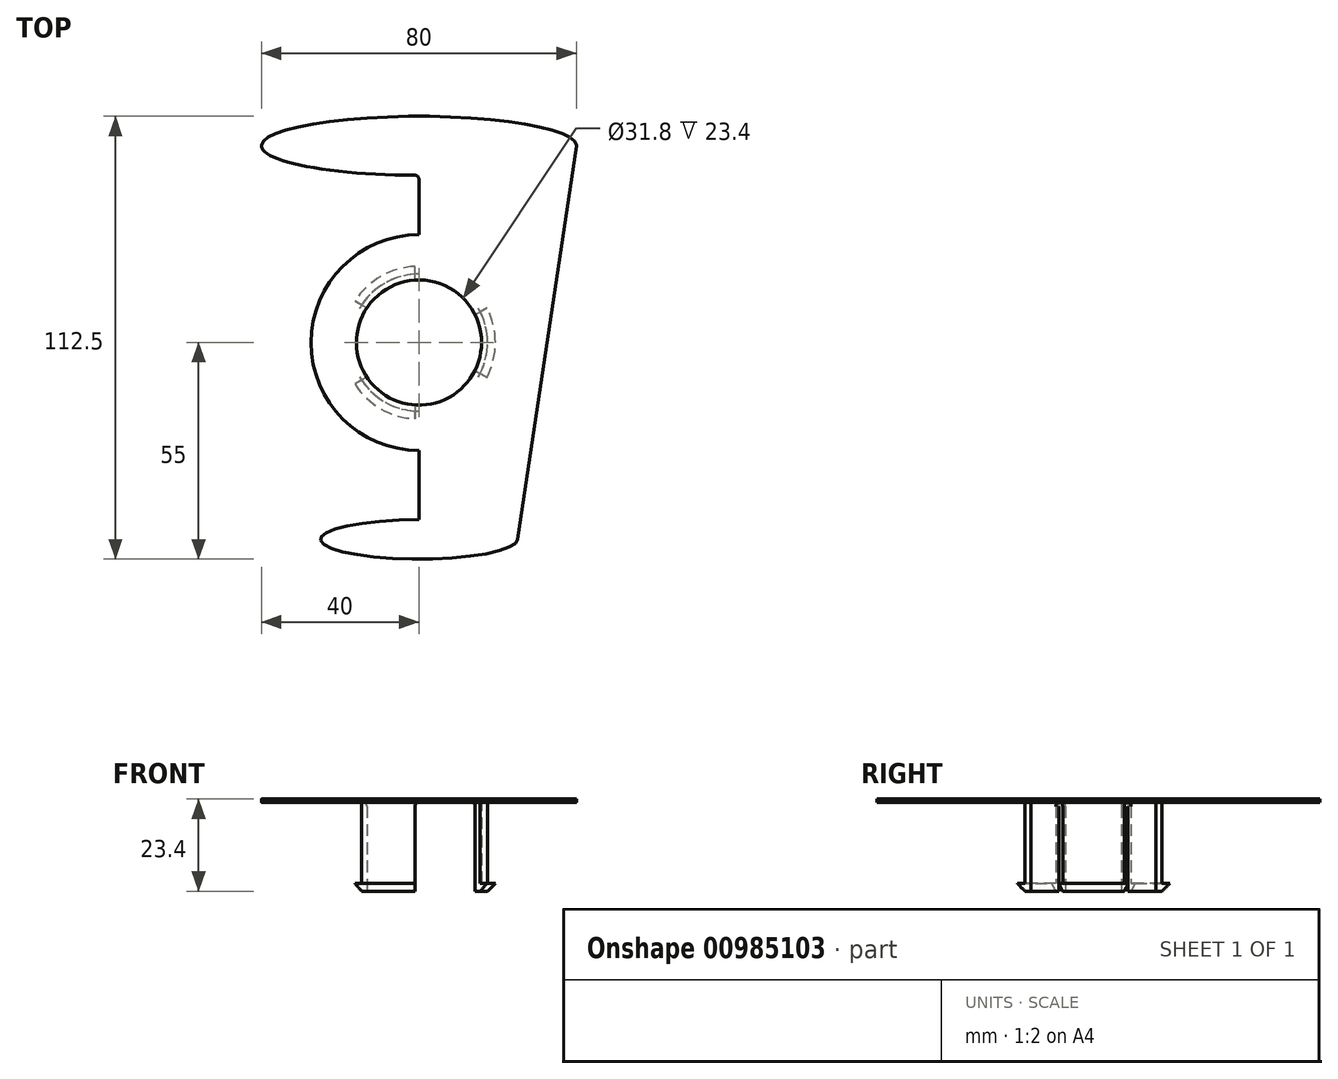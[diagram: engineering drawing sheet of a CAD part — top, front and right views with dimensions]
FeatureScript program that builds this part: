
annotation { "Feature Type Name" : "Feature", "Feature Type Description" : "" }
export const myFeature = defineFeature(function(context is Context, id is Id, definition is map)
    precondition{}
    {
        {
            var Q0;
            Q0=qCreatedBy(makeId("Top.planeOp"),FACE);
            var sketch = newSketch(context, id + "F0", { "sketchPlane" : qUnion([Q0])});
            skCircle(sketch, "E0", {"center": v(0, 0) * mm, "radius": 17.4 * mm});
            skCircle(sketch, "E1", {"center": v(0, 0) * mm, "radius": 15.9 * mm});
            skCircle(sketch, "E2", {"center": v(0, 0) * mm, "radius": 27.4 * mm});
            skLineSegment(sketch, "E3", {"start": v(0, 0) * mm, "end": v(0, 17.75) * mm, "construction": true});
            skText(sketch, "E4", { "text": "o", "fontName": "RobotoSlab-Bold.ttf"});
            skText(sketch, "E5", { "text": "u", "fontName": "RobotoSlab-Bold.ttf"});
            skText(sketch, "E6", { "text": "e", "fontName": "RobotoSlab-Bold.ttf"});
            skText(sketch, "E7", { "text": "i", "fontName": "RobotoSlab-Bold.ttf"});
            skText(sketch, "E8", { "text": "r", "fontName": "RobotoSlab-Bold.ttf"});
            skText(sketch, "E9", { "text": "c", "fontName": "RobotoSlab-Bold.ttf"});
            skText(sketch, "E10", { "text": "e", "fontName": "RobotoSlab-Bold.ttf"});
            skText(sketch, "E11", { "text": "o", "fontName": "RobotoSlab-Bold.ttf"});
            skText(sketch, "E12", { "text": "r", "fontName": "RobotoSlab-Bold.ttf"});
            skText(sketch, "E13", { "text": "n", "fontName": "RobotoSlab-Bold.ttf"});
            skLineSegment(sketch, "E14.2.0", {"start": v(0, 0) * mm, "end": v(-15.37, 8.88) * mm, "construction": true});
            skLineSegment(sketch, "E14.3.0", {"start": v(0, 0) * mm, "end": v(-17.75, 0) * mm, "construction": true});
            skLineSegment(sketch, "E14.4.0", {"start": v(0, 0) * mm, "end": v(-15.37, -8.88) * mm, "construction": true});
            skLineSegment(sketch, "E14.5.0", {"start": v(0, 0) * mm, "end": v(-8.88, -15.37) * mm, "construction": true});
            skLineSegment(sketch, "E14.6.0", {"start": v(0, 0) * mm, "end": v(0, -17.75) * mm, "construction": true});
            skLineSegment(sketch, "E14.7.0", {"start": v(0, 0) * mm, "end": v(8.87, -15.37) * mm, "construction": true});
            skLineSegment(sketch, "E14.8.0", {"start": v(0, 0) * mm, "end": v(15.37, -8.88) * mm, "construction": true});
            skLineSegment(sketch, "E14.9.0", {"start": v(0, 0) * mm, "end": v(17.75, 0) * mm, "construction": true});
            skLineSegment(sketch, "E14.10.0", {"start": v(0, 0) * mm, "end": v(15.37, 8.87) * mm, "construction": true});
            skLineSegment(sketch, "E14.11.0", {"start": v(0, 0) * mm, "end": v(8.88, 15.37) * mm, "construction": true});
            skText(sketch, "E15", { "text": "S", "fontName": "RobotoSlab-Bold.ttf"});
            skLineSegment(sketch, "E16", {"start": v(0, 0) * mm, "end": v(-8.88, 15.37) * mm, "construction": true});
            const initialGuessF0  = {"E4": [-0.00328, 0.01775, 1, 0, 0.008], "E5": [0.0057, 0.0172, 0.86603, -0.5, 0.008], "E6": [0.01692, -0.0062, -0.5, -0.86603, 0.008], "E7": [-0.0071, -0.0164, -0.86603, 0.5, 0.008], "E8": [-0.01407, -0.01114, -0.5, 0.86603, 0.008], "E9": [0.01775, 0.0031, 0, -1, 0.008], "E10": [0.01156, -0.01382, -0.86603, -0.5, 0.008], "E11": [-0.01775, -0.00328, 0, 1, 0.008], "E12": [0.01407, 0.01114, 0.5, -0.86603, 0.008], "E13": [-0.01726, 0.0056, 0.5, 0.86603, 0.008], "E15": [-0.01195, 0.0136, 0.86603, 0.5, 0.008]};
            skSetInitialGuess(sketch, initialGuessF0);
            skSolve(sketch);
        }
        {
            var Q0;
            Q0=makeQuery(id+"F0.imprint","IMPRINT",FACE,{"disambiguationData":[TD([[makeQuery(id+"F0.imprint","IMPRINT",EDGE,{"derivedFrom":sQuery(id+"F0.wireOp",EDGE,"E0")}),1.0]])]});
            var Q1;
            Q1=makeQuery(id+"F0.imprint","IMPRINT",FACE,{"disambiguationData":[TD([[makeQuery(id+"F0.imprint","IMPRINT",EDGE,{"derivedFrom":sQuery(id+"F0.wireOp",EDGE,"E4.sketch_text.stroke-0")}),-1.0]])]});
            var Q2;
            Q2=makeQuery(id+"F0.imprint","IMPRINT",FACE,{"disambiguationData":[TD([[makeQuery(id+"F0.imprint","IMPRINT",EDGE,{"derivedFrom":sQuery(id+"F0.wireOp",EDGE,"E7.sketch_text.stroke-0")}),-1.0]])]});
            var Q3;
            Q3=makeQuery(id+"F0.imprint","IMPRINT",FACE,{"disambiguationData":[TD([[makeQuery(id+"F0.imprint","IMPRINT",EDGE,{"derivedFrom":sQuery(id+"F0.wireOp",EDGE,"E11.sketch_text.stroke-10")}),1.0]])]});
            var Q4;
            Q4=makeQuery(id+"F0.imprint","IMPRINT",FACE,{"disambiguationData":[TD([[makeQuery(id+"F0.imprint","IMPRINT",EDGE,{"derivedFrom":sQuery(id+"F0.wireOp",EDGE,"E9.sketch_text.stroke-0")}),-1.0]])]});
            var Q5;
            Q5=makeQuery(id+"F0.imprint","IMPRINT",FACE,{"disambiguationData":[TD([[makeQuery(id+"F0.imprint","IMPRINT",EDGE,{"derivedFrom":sQuery(id+"F0.wireOp",EDGE,"E10.sketch_text.stroke-0")}),-1.0]])]});
            var Q6;
            Q6=makeQuery(id+"F0.imprint","IMPRINT",FACE,{"disambiguationData":[TD([[makeQuery(id+"F0.imprint","IMPRINT",EDGE,{"derivedFrom":sQuery(id+"F0.wireOp",EDGE,"E6.sketch_text.stroke-0")}),-1.0]])]});
            var Q7;
            Q7=makeQuery(id+"F0.imprint","IMPRINT",FACE,{"disambiguationData":[TD([[makeQuery(id+"F0.imprint","IMPRINT",EDGE,{"derivedFrom":sQuery(id+"F0.wireOp",EDGE,"E12.sketch_text.stroke-0")}),-1.0]])]});
            var Q8;
            Q8=makeQuery(id+"F0.imprint","IMPRINT",FACE,{"disambiguationData":[TD([[makeQuery(id+"F0.imprint","IMPRINT",EDGE,{"derivedFrom":sQuery(id+"F0.wireOp",EDGE,"E5.sketch_text.stroke-0")}),-1.0]])]});
            var Q9;
            Q9=makeQuery(id+"F0.imprint","IMPRINT",FACE,{"disambiguationData":[TD([[makeQuery(id+"F0.imprint","IMPRINT",EDGE,{"derivedFrom":sQuery(id+"F0.wireOp",EDGE,"E0")}),-1.0]])]});
            var Q10;
            Q10=makeQuery(id+"F0.imprint","IMPRINT",FACE,{"disambiguationData":[TD([[makeQuery(id+"F0.imprint","IMPRINT",EDGE,{"derivedFrom":sQuery(id+"F0.wireOp",EDGE,"E5.sketch_text.stroke-10")}),1.0]])]});
            var Q11;
            Q11=makeQuery(id+"F0.imprint","IMPRINT",FACE,{"disambiguationData":[TD([[makeQuery(id+"F0.imprint","IMPRINT",EDGE,{"derivedFrom":sQuery(id+"F0.wireOp",EDGE,"E13.sketch_text.stroke-0")}),-1.0]])]});
            var Q12;
            Q12=makeQuery(id+"F0.imprint","IMPRINT",FACE,{"disambiguationData":[TD([[makeQuery(id+"F0.imprint","IMPRINT",EDGE,{"derivedFrom":sQuery(id+"F0.wireOp",EDGE,"E8.sketch_text.stroke-0")}),-1.0]])]});
            var Q13;
            Q13=makeQuery(id+"F0.imprint","IMPRINT",FACE,{"disambiguationData":[TD([[makeQuery(id+"F0.imprint","IMPRINT",EDGE,{"derivedFrom":sQuery(id+"F0.wireOp",EDGE,"E11.sketch_text.stroke-0")}),-1.0]])]});
            var Q14;
            Q14=makeQuery(id+"F0.imprint","IMPRINT",FACE,{"disambiguationData":[TD([[makeQuery(id+"F0.imprint","IMPRINT",EDGE,{"derivedFrom":sQuery(id+"F0.wireOp",EDGE,"E7.sketch_text.stroke-10")}),-1.0]])]});
            var Q15;
            Q15=makeQuery(id+"F0.imprint","IMPRINT",FACE,{"disambiguationData":[TD([[makeQuery(id+"F0.imprint","IMPRINT",EDGE,{"derivedFrom":sQuery(id+"F0.wireOp",EDGE,"E10.sketch_text.stroke-17")}),1.0]])]});
            var Q16;
            Q16=makeQuery(id+"F0.imprint","IMPRINT",FACE,{"disambiguationData":[TD([[makeQuery(id+"F0.imprint","IMPRINT",EDGE,{"derivedFrom":sQuery(id+"F0.wireOp",EDGE,"E15.sketch_text.stroke-0")}),-1.0]])]});
            var Q17;
            Q17=makeQuery(id+"F0.imprint","IMPRINT",FACE,{"disambiguationData":[TD([[makeQuery(id+"F0.imprint","IMPRINT",EDGE,{"derivedFrom":sQuery(id+"F0.wireOp",EDGE,"E4.sketch_text.stroke-10")}),1.0]])]});
            var Q18;
            Q18=makeQuery(id+"F0.imprint","IMPRINT",FACE,{"disambiguationData":[TD([[makeQuery(id+"F0.imprint","IMPRINT",EDGE,{"derivedFrom":sQuery(id+"F0.wireOp",EDGE,"E6.sketch_text.stroke-17")}),1.0]])]});
            extrude(context, id + "F1", {"entities" : qUnion([Q0, Q1, Q2, Q3, Q4, Q5, Q6, Q7, Q8, Q9, Q10, Q11, Q12, Q13, Q14, Q15, Q16, Q17, Q18]), "depth" : 0.8 * mm, "offsetDistance" : 25 * mm});
        }
        {
            var Q0;
            Q0=makeQuery(id+"F0.imprint","IMPRINT",FACE,{"disambiguationData":[TD([[makeQuery(id+"F0.imprint","IMPRINT",EDGE,{"derivedFrom":sQuery(id+"F0.wireOp",EDGE,"E0")}),1.0]])]});
            extrude(context, id + "F2", {"entities" : qUnion([Q0]), "operationType" : NewBodyOperationType.ADD, "oppositeDirection" : true, "depth" : 22.6 * mm, "offsetDistance" : 25 * mm});
        }
        {
            var Q0;
            Q0=makeQuery(id+"F2.opExtrude","CAP_FACE",FACE,{"disambiguationData":[OSD([sQuery(id+"F0.wireOp",EDGE,"E0"),sQuery(id+"F0.wireOp",EDGE,"E1")])],"isStart":false});
            var sketch = newSketch(context, id + "F3", { "sketchPlane" : qUnion([Q0])});
            skLineSegment(sketch, "E17.bottom", {"start": v(1, 0) * mm, "end": v(-1, 0) * mm});
            skLineSegment(sketch, "E17.top", {"start": v(1, -20) * mm, "end": v(-1, -20) * mm});
            skLineSegment(sketch, "E17.left", {"start": v(1, 0) * mm, "end": v(1, -20) * mm});
            skLineSegment(sketch, "E17.right", {"start": v(-1, 0) * mm, "end": v(-1, -20) * mm});
            skLineSegment(sketch, "E18.1.0", {"start": v(0.5, 0.87) * mm, "end": v(-0.5, -0.87) * mm});
            skLineSegment(sketch, "E18.1.1", {"start": v(17.82, -9.13) * mm, "end": v(16.82, -10.87) * mm});
            skLineSegment(sketch, "E18.1.2", {"start": v(-0.5, -0.87) * mm, "end": v(16.82, -10.87) * mm});
            skLineSegment(sketch, "E18.1.3", {"start": v(0.5, 0.87) * mm, "end": v(17.82, -9.13) * mm});
            skLineSegment(sketch, "E18.2.0", {"start": v(-0.5, 0.87) * mm, "end": v(0.5, -0.87) * mm});
            skLineSegment(sketch, "E18.2.1", {"start": v(16.82, 10.87) * mm, "end": v(17.82, 9.13) * mm});
            skLineSegment(sketch, "E18.2.2", {"start": v(0.5, -0.87) * mm, "end": v(17.82, 9.13) * mm});
            skLineSegment(sketch, "E18.2.3", {"start": v(-0.5, 0.87) * mm, "end": v(16.82, 10.87) * mm});
            skLineSegment(sketch, "E18.3.0", {"start": v(-1, 0) * mm, "end": v(1, 0) * mm});
            skLineSegment(sketch, "E18.3.1", {"start": v(-1, 20) * mm, "end": v(1, 20) * mm});
            skLineSegment(sketch, "E18.3.2", {"start": v(1, 0) * mm, "end": v(1, 20) * mm});
            skLineSegment(sketch, "E18.3.3", {"start": v(-1, 0) * mm, "end": v(-1, 20) * mm});
            skLineSegment(sketch, "E18.4.0", {"start": v(-0.5, -0.87) * mm, "end": v(0.5, 0.87) * mm});
            skLineSegment(sketch, "E18.4.1", {"start": v(-17.82, 9.13) * mm, "end": v(-16.82, 10.87) * mm});
            skLineSegment(sketch, "E18.4.2", {"start": v(0.5, 0.87) * mm, "end": v(-16.82, 10.87) * mm});
            skLineSegment(sketch, "E18.4.3", {"start": v(-0.5, -0.87) * mm, "end": v(-17.82, 9.13) * mm});
            skLineSegment(sketch, "E18.5.0", {"start": v(0.5, -0.87) * mm, "end": v(-0.5, 0.87) * mm});
            skLineSegment(sketch, "E18.5.1", {"start": v(-16.82, -10.87) * mm, "end": v(-17.82, -9.13) * mm});
            skLineSegment(sketch, "E18.5.2", {"start": v(-0.5, 0.87) * mm, "end": v(-17.82, -9.13) * mm});
            skLineSegment(sketch, "E18.5.3", {"start": v(0.5, -0.87) * mm, "end": v(-16.82, -10.87) * mm});
            skPoint(sketch, "E18.center", {"position": v(0, 0) * mm});
            skCircle(sketch, "E19", {"center": v(0, 0) * mm, "radius": 19.4 * mm});
            skSolve(sketch);
        }
        {
            var Q0;
            {var subQ0=sQuery(id+"F3.wireOp",EDGE,"E18.1.2");var subQ1=makeQuery(id+"F2.opExtrude","CAP_EDGE",EDGE,{"disambiguationData":[OSD([sQuery(id+"F0.wireOp",EDGE,"E1")])],"isStart":false});var subQ2=makeQuery(id+"F3.imprint","INTERSECT",VERTEX,{"derivedFrom":[subQ1,subQ0]});Q0=makeQuery(id+"F3.imprint","IMPRINT",FACE,{"disambiguationData":[TD([[makeQuery(id+"F3.imprint","IMPRINT",EDGE,{"disambiguationData":[TD([[subQ2,-1.0]])],"derivedFrom":subQ0}),1.0]])]});}
            var Q1;
            {var subQ0=sQuery(id+"F3.wireOp",EDGE,"E17.left");var subQ1=makeQuery(id+"F2.opExtrude","CAP_EDGE",EDGE,{"disambiguationData":[OSD([sQuery(id+"F0.wireOp",EDGE,"E1")])],"isStart":false});var subQ2=makeQuery(id+"F3.imprint","INTERSECT",VERTEX,{"derivedFrom":[subQ1,subQ0]});Q1=makeQuery(id+"F3.imprint","IMPRINT",FACE,{"disambiguationData":[TD([[makeQuery(id+"F3.imprint","IMPRINT",EDGE,{"disambiguationData":[TD([[subQ2,-1.0]])],"derivedFrom":subQ0}),-1.0]])]});}
            var Q2;
            {var subQ0=sQuery(id+"F3.wireOp",EDGE,"E18.5.2");var subQ1=makeQuery(id+"F2.opExtrude","CAP_EDGE",EDGE,{"disambiguationData":[OSD([sQuery(id+"F0.wireOp",EDGE,"E1")])],"isStart":false});var subQ2=makeQuery(id+"F3.imprint","INTERSECT",VERTEX,{"derivedFrom":[subQ1,subQ0]});Q2=makeQuery(id+"F3.imprint","IMPRINT",FACE,{"disambiguationData":[TD([[makeQuery(id+"F3.imprint","IMPRINT",EDGE,{"disambiguationData":[TD([[subQ2,-1.0]])],"derivedFrom":subQ0}),1.0]])]});}
            var Q3;
            {var subQ0=sQuery(id+"F3.wireOp",EDGE,"E18.4.2");var subQ1=makeQuery(id+"F2.opExtrude","CAP_EDGE",EDGE,{"disambiguationData":[OSD([sQuery(id+"F0.wireOp",EDGE,"E1")])],"isStart":false});var subQ2=makeQuery(id+"F3.imprint","INTERSECT",VERTEX,{"derivedFrom":[subQ1,subQ0]});Q3=makeQuery(id+"F3.imprint","IMPRINT",FACE,{"disambiguationData":[TD([[makeQuery(id+"F3.imprint","IMPRINT",EDGE,{"disambiguationData":[TD([[subQ2,-1.0]])],"derivedFrom":subQ0}),1.0]])]});}
            var Q4;
            {var subQ0=sQuery(id+"F3.wireOp",EDGE,"E18.3.2");var subQ1=makeQuery(id+"F2.opExtrude","CAP_EDGE",EDGE,{"disambiguationData":[OSD([sQuery(id+"F0.wireOp",EDGE,"E1")])],"isStart":false});var subQ2=makeQuery(id+"F3.imprint","INTERSECT",VERTEX,{"derivedFrom":[subQ1,subQ0]});Q4=makeQuery(id+"F3.imprint","IMPRINT",FACE,{"disambiguationData":[TD([[makeQuery(id+"F3.imprint","IMPRINT",EDGE,{"disambiguationData":[TD([[subQ2,-1.0]])],"derivedFrom":subQ0}),1.0]])]});}
            var Q5;
            {var subQ0=sQuery(id+"F3.wireOp",EDGE,"E18.2.2");var subQ1=makeQuery(id+"F2.opExtrude","CAP_EDGE",EDGE,{"disambiguationData":[OSD([sQuery(id+"F0.wireOp",EDGE,"E1")])],"isStart":false});var subQ2=makeQuery(id+"F3.imprint","INTERSECT",VERTEX,{"derivedFrom":[subQ1,subQ0]});Q5=makeQuery(id+"F3.imprint","IMPRINT",FACE,{"disambiguationData":[TD([[makeQuery(id+"F3.imprint","IMPRINT",EDGE,{"disambiguationData":[TD([[subQ2,-1.0]])],"derivedFrom":subQ0}),1.0]])]});}
            var Q6;
            {var subQ0=sQuery(id+"F3.wireOp",EDGE,"E17.left");var subQ1=makeQuery(id+"F2.opExtrude","CAP_EDGE",EDGE,{"disambiguationData":[OSD([sQuery(id+"F0.wireOp",EDGE,"E1")])],"isStart":false});var subQ2=makeQuery(id+"F3.imprint","INTERSECT",VERTEX,{"derivedFrom":[subQ1,subQ0]});Q6=makeQuery(id+"F3.imprint","IMPRINT",FACE,{"disambiguationData":[TD([[makeQuery(id+"F3.imprint","IMPRINT",EDGE,{"disambiguationData":[TD([[subQ2,-1.0]])],"derivedFrom":subQ0}),1.0]])]});}
            var Q7;
            {var subQ0=sQuery(id+"F3.wireOp",EDGE,"E18.4.3");var subQ1=makeQuery(id+"F2.opExtrude","CAP_EDGE",EDGE,{"disambiguationData":[OSD([sQuery(id+"F0.wireOp",EDGE,"E1")])],"isStart":false});var subQ2=makeQuery(id+"F3.imprint","INTERSECT",VERTEX,{"derivedFrom":[subQ1,subQ0]});Q7=makeQuery(id+"F3.imprint","IMPRINT",FACE,{"disambiguationData":[TD([[makeQuery(id+"F3.imprint","IMPRINT",EDGE,{"disambiguationData":[TD([[subQ2,-1.0]])],"derivedFrom":subQ0}),1.0]])]});}
            var Q8;
            {var subQ0=sQuery(id+"F3.wireOp",EDGE,"E18.2.3");var subQ1=makeQuery(id+"F2.opExtrude","CAP_EDGE",EDGE,{"disambiguationData":[OSD([sQuery(id+"F0.wireOp",EDGE,"E1")])],"isStart":false});var subQ2=makeQuery(id+"F3.imprint","INTERSECT",VERTEX,{"derivedFrom":[subQ1,subQ0]});Q8=makeQuery(id+"F3.imprint","IMPRINT",FACE,{"disambiguationData":[TD([[makeQuery(id+"F3.imprint","IMPRINT",EDGE,{"disambiguationData":[TD([[subQ2,-1.0]])],"derivedFrom":subQ0}),1.0]])]});}
            var Q9;
            Q9=makeQuery(id+"F1.opExtrude","CAP_FACE",FACE,{"disambiguationData":[OSD([sQuery(id+"F0.wireOp",EDGE,"E1"),sQuery(id+"F0.wireOp",EDGE,"E2")])],"isStart":true});
            extrude(context, id + "F4", {"entities" : qUnion([Q0, Q1, Q2, Q3, Q4, Q5, Q6, Q7, Q8]), "operationType" : NewBodyOperationType.REMOVE, "endBound" : BoundingType.UP_TO_SURFACE, "oppositeDirection" : true, "depth" : 25 * mm, "endBoundEntityFace" : qUnion([Q9]), "offsetDistance" : 25 * mm});
        }
        {
            var Q0;
            {var subQ0=sQuery(id+"F3.wireOp",EDGE,"E19");var subQ1=sQuery(id+"F3.wireOp",EDGE,"E18.1.3");var subQ2=makeQuery(id+"F3.imprint","INTERSECT",VERTEX,{"derivedFrom":[subQ1,subQ0]});Q0=makeQuery(id+"F3.imprint","IMPRINT",FACE,{"disambiguationData":[TD([[makeQuery(id+"F3.imprint","IMPRINT",EDGE,{"disambiguationData":[TD([[subQ2,1.0]])],"derivedFrom":subQ1}),1.0]])]});}
            var Q1;
            {var subQ0=sQuery(id+"F3.wireOp",EDGE,"E19");var subQ1=sQuery(id+"F3.wireOp",EDGE,"E17.right");var subQ2=makeQuery(id+"F3.imprint","INTERSECT",VERTEX,{"derivedFrom":[subQ1,subQ0]});Q1=makeQuery(id+"F3.imprint","IMPRINT",FACE,{"disambiguationData":[TD([[makeQuery(id+"F3.imprint","IMPRINT",EDGE,{"disambiguationData":[TD([[subQ2,1.0]])],"derivedFrom":subQ1}),-1.0]])]});}
            var Q2;
            {var subQ0=sQuery(id+"F3.wireOp",EDGE,"E19");var subQ1=sQuery(id+"F3.wireOp",EDGE,"E18.3.3");var subQ2=makeQuery(id+"F3.imprint","INTERSECT",VERTEX,{"derivedFrom":[subQ1,subQ0]});Q2=makeQuery(id+"F3.imprint","IMPRINT",FACE,{"disambiguationData":[TD([[makeQuery(id+"F3.imprint","IMPRINT",EDGE,{"disambiguationData":[TD([[subQ2,1.0]])],"derivedFrom":subQ1}),1.0]])]});}
            extrude(context, id + "F5", {"entities" : qUnion([Q0, Q1, Q2]), "operationType" : NewBodyOperationType.ADD, "oppositeDirection" : true, "depth" : 2 * mm, "offsetDistance" : 25 * mm});
        }
        {
            var Q0;
            {var subQ0=sQuery(id+"F3.wireOp",EDGE,"E19");Q0=makeQuery(id+"F5.opExtrude","CAP_EDGE",EDGE,{"disambiguationData":[OSD([subQ0]),TDD([makeQuery(id+"F3.imprint","IMPRINT",EDGE,{"disambiguationData":[TD([[makeQuery(id+"F3.imprint","INTERSECT",VERTEX,{"derivedFrom":[sQuery(id+"F3.wireOp",EDGE,"E18.1.3"),subQ0]}),-1.0]])],"derivedFrom":subQ0})])],"isStart":true});}
            var Q1;
            {var subQ0=sQuery(id+"F3.wireOp",EDGE,"E19");Q1=makeQuery(id+"F5.opExtrude","CAP_EDGE",EDGE,{"disambiguationData":[OSD([subQ0]),TDD([makeQuery(id+"F3.imprint","IMPRINT",EDGE,{"disambiguationData":[TD([[makeQuery(id+"F3.imprint","INTERSECT",VERTEX,{"derivedFrom":[sQuery(id+"F3.wireOp",EDGE,"E18.2.3"),subQ0]}),-1.0]])],"derivedFrom":subQ0})])],"isStart":true});}
            var Q2;
            {var subQ0=sQuery(id+"F3.wireOp",EDGE,"E19");Q2=makeQuery(id+"F5.opExtrude","CAP_EDGE",EDGE,{"disambiguationData":[OSD([subQ0]),TDD([makeQuery(id+"F3.imprint","IMPRINT",EDGE,{"disambiguationData":[TD([[makeQuery(id+"F3.imprint","INTERSECT",VERTEX,{"derivedFrom":[sQuery(id+"F3.wireOp",EDGE,"E18.3.3"),subQ0]}),-1.0]])],"derivedFrom":subQ0})])],"isStart":true});}
            var Q3;
            {var subQ0=sQuery(id+"F3.wireOp",EDGE,"E19");Q3=makeQuery(id+"F5.opExtrude","CAP_EDGE",EDGE,{"disambiguationData":[OSD([subQ0]),TDD([makeQuery(id+"F3.imprint","IMPRINT",EDGE,{"disambiguationData":[TD([[makeQuery(id+"F3.imprint","INTERSECT",VERTEX,{"derivedFrom":[sQuery(id+"F3.wireOp",EDGE,"E17.right"),subQ0]}),1.0]])],"derivedFrom":subQ0})])],"isStart":true});}
            var Q4;
            {var subQ0=sQuery(id+"F3.wireOp",EDGE,"E19");Q4=makeQuery(id+"F5.opExtrude","CAP_EDGE",EDGE,{"disambiguationData":[OSD([subQ0]),TDD([makeQuery(id+"F3.imprint","IMPRINT",EDGE,{"disambiguationData":[TD([[makeQuery(id+"F3.imprint","INTERSECT",VERTEX,{"derivedFrom":[sQuery(id+"F3.wireOp",EDGE,"E17.left"),subQ0]}),-1.0]])],"derivedFrom":subQ0})])],"isStart":true});}
            var Q5;
            {var subQ0=sQuery(id+"F3.wireOp",EDGE,"E19");Q5=makeQuery(id+"F5.opExtrude","CAP_EDGE",EDGE,{"disambiguationData":[OSD([subQ0]),TDD([makeQuery(id+"F3.imprint","IMPRINT",EDGE,{"disambiguationData":[TD([[makeQuery(id+"F3.imprint","INTERSECT",VERTEX,{"derivedFrom":[sQuery(id+"F3.wireOp",EDGE,"E18.4.3"),subQ0]}),-1.0]])],"derivedFrom":subQ0})])],"isStart":true});}
            chamfer(context, id + "F6", {"entities" : qUnion([Q0, Q1, Q2, Q3, Q4, Q5]), "width" : 2 * mm, "tangentPropagation" : true});
        }
        {
            var Q0;
            {var subQ0=sQuery(id+"F3.wireOp",EDGE,"E17.right");var subQ2=sQuery(id+"F0.wireOp",EDGE,"E0");Q0=makeQuery(id+"F4.boolean.opBoolean","SPLIT",EDGE,{"disambiguationData":[TD([makeQuery(id+"F4.opExtrude","SWEPT_FACE",FACE,{"disambiguationData":[OSD([subQ0])]})])],"derivedFrom":makeQuery(id+"F2.opExtrude","CAP_EDGE",EDGE,{"disambiguationData":[OSD([subQ2])],"isStart":true})});}
            var Q1;
            {var subQ1=sQuery(id+"F0.wireOp",EDGE,"E0");var subQ2=sQuery(id+"F3.wireOp",EDGE,"E18.3.3");Q1=makeQuery(id+"F4.boolean.opBoolean","SPLIT",EDGE,{"disambiguationData":[TD([makeQuery(id+"F4.opExtrude","SWEPT_FACE",FACE,{"disambiguationData":[OSD([subQ2])]})])],"derivedFrom":makeQuery(id+"F2.opExtrude","CAP_EDGE",EDGE,{"disambiguationData":[OSD([subQ1])],"isStart":true})});}
            var Q2;
            {var subQ0=sQuery(id+"F3.wireOp",EDGE,"E18.1.3");var subQ2=sQuery(id+"F0.wireOp",EDGE,"E0");Q2=makeQuery(id+"F4.boolean.opBoolean","SPLIT",EDGE,{"disambiguationData":[TD([makeQuery(id+"F4.opExtrude","SWEPT_FACE",FACE,{"disambiguationData":[OSD([subQ0])]})])],"derivedFrom":makeQuery(id+"F2.opExtrude","CAP_EDGE",EDGE,{"disambiguationData":[OSD([subQ2])],"isStart":true})});}
            var Q3;
            Q3=makeQuery(id+"F4.boolean.opBoolean","COPY",EDGE,{"derivedFrom":makeQuery(id+"F4.opExtrude","CAP_EDGE",EDGE,{"disambiguationData":[OSD([sQuery(id+"F3.wireOp",EDGE,"E18.2.2")])],"isStart":false})});
            var Q4;
            Q4=makeQuery(id+"F4.boolean.opBoolean","COPY",EDGE,{"derivedFrom":makeQuery(id+"F4.opExtrude","CAP_EDGE",EDGE,{"disambiguationData":[OSD([sQuery(id+"F3.wireOp",EDGE,"E18.3.3")])],"isStart":false})});
            var Q5;
            Q5=makeQuery(id+"F4.boolean.opBoolean","COPY",EDGE,{"derivedFrom":makeQuery(id+"F4.opExtrude","CAP_EDGE",EDGE,{"disambiguationData":[OSD([sQuery(id+"F3.wireOp",EDGE,"E18.1.3")])],"isStart":false})});
            var Q6;
            Q6=makeQuery(id+"F4.boolean.opBoolean","COPY",EDGE,{"derivedFrom":makeQuery(id+"F4.opExtrude","CAP_EDGE",EDGE,{"disambiguationData":[OSD([sQuery(id+"F3.wireOp",EDGE,"E17.right")])],"isStart":false})});
            var Q7;
            Q7=makeQuery(id+"F4.boolean.opBoolean","COPY",EDGE,{"derivedFrom":makeQuery(id+"F4.opExtrude","CAP_EDGE",EDGE,{"disambiguationData":[OSD([sQuery(id+"F3.wireOp",EDGE,"E18.5.3")])],"isStart":false})});
            var Q8;
            Q8=makeQuery(id+"F4.boolean.opBoolean","COPY",EDGE,{"derivedFrom":makeQuery(id+"F4.opExtrude","CAP_EDGE",EDGE,{"disambiguationData":[OSD([sQuery(id+"F3.wireOp",EDGE,"E18.4.2")])],"isStart":false})});
            fillet(context, id + "F7", {"entities" : qUnion([Q0, Q1, Q2, Q3, Q4, Q5, Q6, Q7, Q8]), "radius" : 1 * mm, "tangentPropagation" : true, "allowEdgeOverflow" : false});
        }
        {
            var Q0;
            Q0=makeQuery(id+"F1.opExtrude","CAP_FACE",FACE,{"disambiguationData":[OSD([sQuery(id+"F0.wireOp",EDGE,"E1"),sQuery(id+"F0.wireOp",EDGE,"E2")])],"isStart":false});
            var sketch = newSketch(context, id + "F8", { "sketchPlane" : qUnion([Q0])});
            skLineSegment(sketch, "E20", {"start": v(0, 50) * mm, "end": v(0, -50) * mm});
            skEllipse(sketch, "E21", {"center": v(0, 50) * mm, "majorRadius": 40 * mm, "minorRadius": 7.5 * mm, "majorAxis": v(-1, 0)});
            skEllipse(sketch, "E22", {"center": v(0, -50) * mm, "majorRadius": 25 * mm, "minorRadius": 5 * mm, "majorAxis": v(-1, 0)});
            skLineSegment(sketch, "E23", {"start": v(-40, 50) * mm, "end": v(-25, -50) * mm});
            skLineSegment(sketch, "E24", {"start": v(25, -50) * mm, "end": v(40, 50) * mm});
            skFitSpline(sketch, "E25.0", {"points": [v(-41.92, 50.9) * mm, v(-42.04, 50) * mm, v(-41.92, 49.1) * mm, v(-41.6, 48.3) * mm, v(-41.14, 47.63) * mm, v(-40.42, 46.87) * mm, v(-39.36, 46.1) * mm, v(-37.83, 45.3) * mm, v(-36, 44.57) * mm, v(-33.87, 43.9) * mm, v(-31.84, 43.4) * mm, v(-30.07, 43) * mm, v(-28.66, 42.73) * mm, v(-27.2, 42.47) * mm, v(-25.15, 42.14) * mm, v(-22.47, 41.76) * mm, v(-19.06, 41.38) * mm, v(-15.49, 41.07) * mm, v(-11.77, 40.82) * mm, v(-7.93, 40.64) * mm, v(-4.66, 40.54) * mm, v(-2, 40.5) * mm, v(0, 40.5) * mm, v(2, 40.5) * mm, v(4.66, 40.54) * mm, v(7.93, 40.64) * mm, v(11.77, 40.82) * mm, v(15.49, 41.07) * mm, v(19.06, 41.38) * mm, v(22.47, 41.76) * mm, v(25.15, 42.14) * mm, v(27.2, 42.47) * mm, v(28.66, 42.73) * mm, v(30.07, 43) * mm, v(31.84, 43.4) * mm, v(33.87, 43.9) * mm, v(36, 44.57) * mm, v(37.83, 45.3) * mm, v(39.36, 46.1) * mm, v(40.42, 46.87) * mm, v(41.14, 47.63) * mm, v(41.6, 48.3) * mm, v(41.92, 49.1) * mm, v(42.04, 50) * mm, v(41.92, 50.9) * mm, v(41.6, 51.7) * mm, v(41.14, 52.37) * mm, v(40.42, 53.13) * mm, v(39.36, 53.9) * mm, v(37.83, 54.7) * mm, v(36, 55.43) * mm, v(33.87, 56.1) * mm, v(31.84, 56.6) * mm, v(30.07, 57) * mm, v(28.66, 57.27) * mm, v(27.2, 57.53) * mm, v(25.15, 57.86) * mm, v(22.47, 58.24) * mm, v(19.06, 58.62) * mm, v(15.49, 58.93) * mm, v(11.77, 59.18) * mm, v(7.93, 59.36) * mm, v(4.66, 59.46) * mm, v(2, 59.5) * mm, v(0, 59.5) * mm, v(-2, 59.5) * mm, v(-4.66, 59.46) * mm, v(-7.93, 59.36) * mm, v(-11.77, 59.18) * mm, v(-15.49, 58.93) * mm, v(-19.06, 58.62) * mm, v(-22.47, 58.24) * mm, v(-25.15, 57.86) * mm, v(-27.2, 57.53) * mm, v(-28.66, 57.27) * mm, v(-30.07, 57) * mm, v(-31.84, 56.6) * mm, v(-33.87, 56.1) * mm, v(-36, 55.43) * mm, v(-37.83, 54.7) * mm, v(-39.36, 53.9) * mm, v(-40.42, 53.13) * mm, v(-41.14, 52.37) * mm, v(-41.6, 51.7) * mm, v(-41.92, 50.9) * mm, v(-42.04, 50) * mm, v(-41.92, 49.1) * mm, v(-41.92, 50.9) * mm]});
            skLineSegment(sketch, "E26", {"start": v(-20, 43.5) * mm, "end": v(-20, 41.5) * mm});
            skLineSegment(sketch, "E27.MirrorCS", {"start": v(20, 43.5) * mm, "end": v(20, 41.5) * mm});
            skSolve(sketch);
        }
        {
            var Q0;
            {var subQ1=sQuery(id+"F8.wireOp",EDGE,"LKSQvbUb-MPd7-Romt-59ob-79xopyYvKsII.bottom");var subQ6=makeQuery(id+"F1.opExtrude","CAP_EDGE",EDGE,{"disambiguationData":[OSD([sQuery(id+"F0.wireOp",EDGE,"E2")])],"isStart":false});var subQ8=makeQuery(id+"F8.imprint","INTERSECT",VERTEX,{"disambiguationData":[OD(0.0)],"derivedFrom":[subQ6,subQ1]});Q0=makeQuery(id+"F8.imprint","IMPRINT",FACE,{"disambiguationData":[TD([[makeQuery(id+"F8.imprint","IMPRINT",EDGE,{"disambiguationData":[TD([[subQ8,1.0]])],"derivedFrom":subQ6}),-1.0]])]});}
            var Q1;
            {var subQ2=sQuery(id+"F8.wireOp",EDGE,"inkod72N-38P0-aWG3-HRaY-s0Pa3sIcXFIJ");Q1=makeQuery(id+"F8.imprint","IMPRINT",FACE,{"disambiguationData":[TD([[makeQuery(id+"F8.imprint","IMPRINT",EDGE,{"derivedFrom":subQ2}),-1.0]])]});}
            var Q2;
            {var subQ1=sQuery(id+"F8.wireOp",EDGE,"inkod72N-38P0-aWG3-HRaY-s0Pa3sIcXFIJ");Q2=makeQuery(id+"F8.imprint","IMPRINT",FACE,{"disambiguationData":[TD([[makeQuery(id+"F8.imprint","IMPRINT",EDGE,{"derivedFrom":subQ1}),1.0]])]});}
            var Q3;
            Q3=makeQuery(id+"F8.imprint","IMPRINT",FACE,{"disambiguationData":[TD([[makeQuery(id+"F8.imprint","IMPRINT",EDGE,{"derivedFrom":sQuery(id+"F8.wireOp",EDGE,"SP4VWVge-bMZd-GdyG-8Ddg-jXr0BoRuJnOE.right")}),-1.0]])]});
            var Q4;
            {var subQ0=sQuery(id+"F8.wireOp",EDGE,"SP4VWVge-bMZd-GdyG-8Ddg-jXr0BoRuJnOE.right");Q4=makeQuery(id+"F8.imprint","IMPRINT",FACE,{"disambiguationData":[TD([[makeQuery(id+"F8.imprint","IMPRINT",EDGE,{"derivedFrom":subQ0}),1.0]])]});}
            var Q5;
            Q5=makeQuery(id+"F8.imprint","IMPRINT",FACE,{"disambiguationData":[TD([[makeQuery(id+"F8.imprint","IMPRINT",EDGE,{"derivedFrom":sQuery(id+"F8.wireOp",EDGE,"LKSQvbUb-MPd7-Romt-59ob-79xopyYvKsII.right")}),1.0]])]});
            var Q6;
            Q6=makeQuery(id+"F8.imprint","IMPRINT",FACE,{"disambiguationData":[TD([[makeQuery(id+"F8.imprint","IMPRINT",EDGE,{"derivedFrom":sQuery(id+"F8.wireOp",EDGE,"SP4VWVge-bMZd-GdyG-8Ddg-jXr0BoRuJnOE.left")}),-1.0]])]});
            var Q7;
            {var subQ1=sQuery(id+"F8.wireOp",EDGE,"E21");var subQ6=makeQuery(id+"F8.imprint","INTERSECT",VERTEX,{"derivedFrom":[sQuery(id+"F8.wireOp",EDGE,"E20"),subQ1]});Q7=makeQuery(id+"F8.imprint","IMPRINT",FACE,{"disambiguationData":[TD([[makeQuery(id+"F8.imprint","IMPRINT",EDGE,{"disambiguationData":[TD([[subQ6,1.0]])],"derivedFrom":subQ1}),1.0]])]});}
            var Q8;
            {var subQ0=sQuery(id+"F8.wireOp",EDGE,"E22");var subQ1=makeQuery(id+"F8.imprint","INTERSECT",VERTEX,{"derivedFrom":[subQ0,sQuery(id+"F8.wireOp",EDGE,"E23")]});Q8=makeQuery(id+"F8.imprint","IMPRINT",FACE,{"disambiguationData":[TD([[makeQuery(id+"F8.imprint","IMPRINT",EDGE,{"disambiguationData":[TD([[subQ1,-1.0]])],"derivedFrom":subQ0}),1.0]])]});}
            var Q9;
            {var subQ3=sQuery(id+"F8.wireOp",EDGE,"E25.0");var subQ5=sQuery(id+"F8.wireOp",EDGE,"E20");var subQ10=makeQuery(id+"F8.imprint","INTERSECT",VERTEX,{"derivedFrom":[subQ5,subQ3]});Q9=makeQuery(id+"F8.imprint","IMPRINT",FACE,{"disambiguationData":[TD([[makeQuery(id+"F8.imprint","IMPRINT",EDGE,{"disambiguationData":[TD([[subQ10,-1.0]])],"derivedFrom":subQ5}),-1.0]])]});}
            var Q10;
            {var subQ0=sQuery(id+"F8.wireOp",EDGE,"E27.MirrorCS");Q10=makeQuery(id+"F8.imprint","IMPRINT",FACE,{"disambiguationData":[TD([[makeQuery(id+"F8.imprint","IMPRINT",EDGE,{"derivedFrom":subQ0}),1.0]])]});}
            var Q11;
            {var subQ0=sQuery(id+"F0.wireOp",EDGE,"E1");var subQ1=sQuery(id+"F0.wireOp",EDGE,"E0");Q11=makeQuery(id+"F4.boolean.opBoolean","MERGE",FACE,{"derivedFrom":[makeQuery(id+"F1.opExtrude","CAP_FACE",FACE,{"disambiguationData":[OSD([subQ0,sQuery(id+"F0.wireOp",EDGE,"E2")])],"isStart":true})],"fromTools":[makeQuery(id+"F4.opExtrude","CAP_FACE",FACE,{"disambiguationData":[OSD([subQ1,subQ0,sQuery(id+"F3.wireOp",EDGE,"E17.right"),sQuery(id+"F3.wireOp",EDGE,"E18.1.3")])],"isStart":false}),makeQuery(id+"F4.opExtrude","CAP_FACE",FACE,{"disambiguationData":[OSD([subQ1,subQ0,sQuery(id+"F3.wireOp",EDGE,"E18.2.2"),sQuery(id+"F3.wireOp",EDGE,"E18.3.3")])],"isStart":false}),makeQuery(id+"F4.opExtrude","CAP_FACE",FACE,{"disambiguationData":[OSD([subQ1,subQ0,sQuery(id+"F3.wireOp",EDGE,"E18.4.2"),sQuery(id+"F3.wireOp",EDGE,"E18.5.3")])],"isStart":false})]});}
            extrude(context, id + "F9", {"entities" : qUnion([Q0, Q1, Q2, Q3, Q4, Q5, Q6, Q7, Q8, Q9, Q10]), "operationType" : NewBodyOperationType.ADD, "endBound" : BoundingType.UP_TO_SURFACE, "oppositeDirection" : true, "depth" : 25 * mm, "endBoundEntityFace" : qUnion([Q11]), "offsetDistance" : 25 * mm});
        }
        {
            var Q0;
            Q0=makeQuery(id+"F9.opExtrude","SWEPT_EDGE",EDGE,{"disambiguationData":[OSD([sQuery(id+"F8.wireOp",EDGE,"E21"),sQuery(id+"F8.wireOp",EDGE,"E27.MirrorCS")])]});
            var Q1;
            Q1=makeQuery(id+"F9.opExtrude","SWEPT_EDGE",EDGE,{"disambiguationData":[OSD([sQuery(id+"F8.wireOp",EDGE,"E25.0"),sQuery(id+"F8.wireOp",EDGE,"E27.MirrorCS")])]});
            fillet(context, id + "F10", {"entities" : qUnion([Q0, Q1]), "radius" : 1 * mm, "tangentPropagation" : true, "allowEdgeOverflow" : false});
        }
    });
